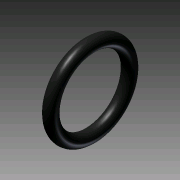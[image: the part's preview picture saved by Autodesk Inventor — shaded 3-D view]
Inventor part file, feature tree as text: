
AUTODESK INVENTOR PART (.ipt)
format: ipt  version: 2011 (Build 150239000, 239)  size: 95,232 bytes
history: native  units: in
note: dims shown in document units (in); Inventor stores cm internally (conversion verified against a paired STEP export)
features: revolve x1, sketch x1
ambient origin geometry x8: Origin, YZ Plane, XZ Plane, XY Plane, X Axis, Y Axis, Z Axis, Center Point
bodies: Solid1 (feature_tree)
feature tree (2):
  revolve  "Revolution1"  [1 undecoded]
  sketch  "Sketch1"  dims[d0=0.125in d1=0.3355in d2=90.0deg]
note: 1 required parameter value undecoded (feature->parameter linkage not recoverable at this tier; creation-order binding heuristic only, values carry confidence <= 0.55)
